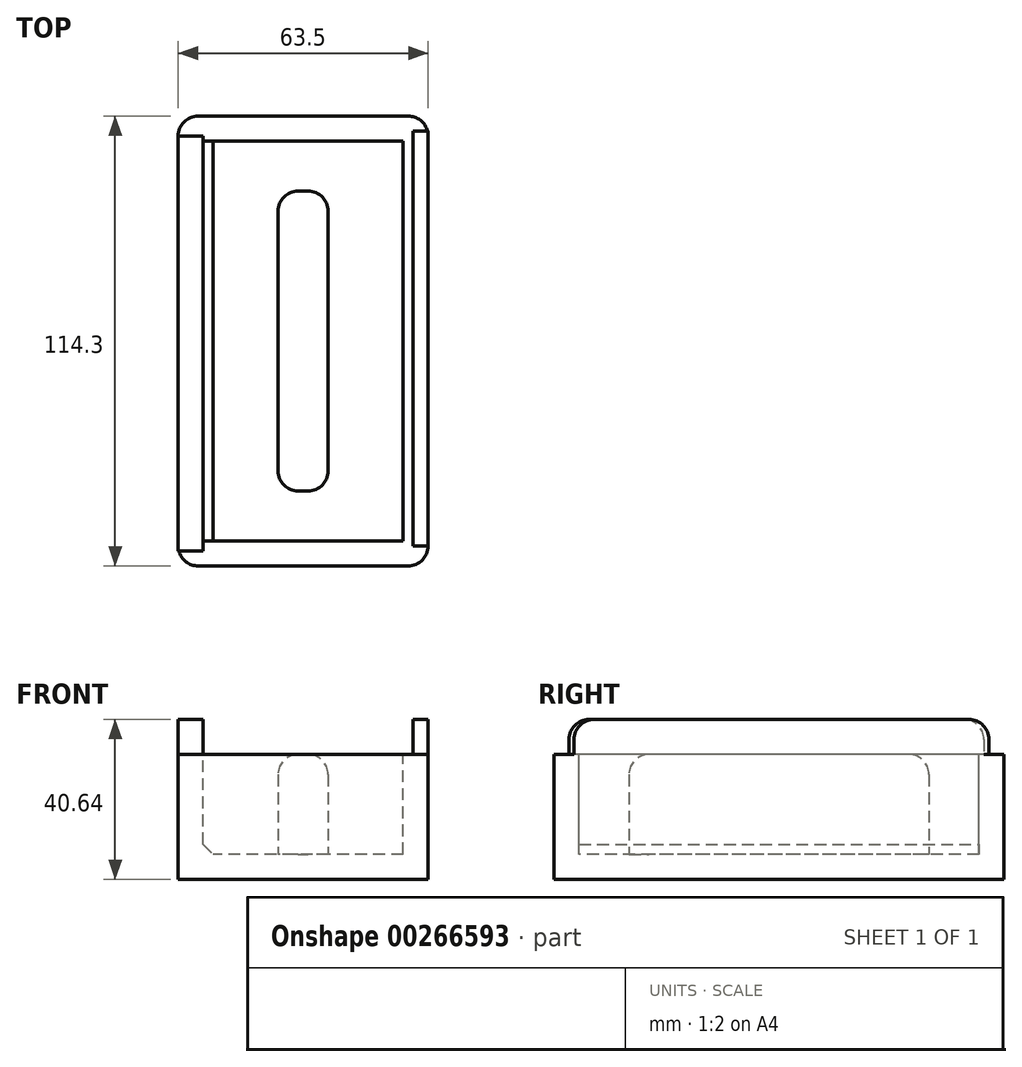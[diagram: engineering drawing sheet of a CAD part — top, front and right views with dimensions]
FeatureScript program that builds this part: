
annotation { "Feature Type Name" : "Feature", "Feature Type Description" : "" }
export const myFeature = defineFeature(function(context is Context, id is Id, definition is map)
    precondition{}
    {
        {
            var Q0;
            Q0=qCreatedBy(makeId("Top.planeOp"),FACE);
            var sketch = newSketch(context, id + "F0", { "sketchPlane" : qUnion([Q0])});
            skLineSegment(sketch, "E0.bottom", {"start": v(-31.75, -57.15) * mm, "end": v(31.75, -57.15) * mm});
            skLineSegment(sketch, "E0.top", {"start": v(-31.75, 57.15) * mm, "end": v(31.75, 57.15) * mm});
            skLineSegment(sketch, "E0.left", {"start": v(-31.75, -57.15) * mm, "end": v(-31.75, 57.15) * mm});
            skLineSegment(sketch, "E0.right", {"start": v(31.75, -57.15) * mm, "end": v(31.75, 57.15) * mm});
            skPoint(sketch, "E0.middle", {"position": v(0, 0) * mm});
            skSolve(sketch);
        }
        {
            var Q0;
            Q0=makeQuery(id+"F0.imprint","IMPRINT",FACE,{"disambiguationData":[TD([[makeQuery(id+"F0.imprint","IMPRINT",EDGE,{"derivedFrom":sQuery(id+"F0.wireOp",EDGE,"E0.bottom")}),1.0]])]});
            extrude(context, id + "F1", {"entities" : qUnion([Q0]), "depth" : 31.75 * mm});
        }
        {
            var Q0;
            Q0=makeQuery(id+"F1.opExtrude","CAP_FACE",FACE,{"disambiguationData":[OSD([sQuery(id+"F0.wireOp",EDGE,"E0.bottom"),sQuery(id+"F0.wireOp",EDGE,"E0.top"),sQuery(id+"F0.wireOp",EDGE,"E0.left"),sQuery(id+"F0.wireOp",EDGE,"E0.right")])],"isStart":false});
            var sketch = newSketch(context, id + "F2", { "sketchPlane" : qUnion([Q0])});
            skLineSegment(sketch, "E1.bottom", {"start": v(25.4, 50.8) * mm, "end": v(-25.4, 50.8) * mm});
            skLineSegment(sketch, "E1.top", {"start": v(25.4, -50.8) * mm, "end": v(-25.4, -50.8) * mm});
            skLineSegment(sketch, "E1.left", {"start": v(25.4, 50.8) * mm, "end": v(25.4, -50.8) * mm});
            skLineSegment(sketch, "E1.right", {"start": v(-25.4, 50.8) * mm, "end": v(-25.4, -50.8) * mm});
            skPoint(sketch, "E1.middle", {"position": v(0, 0) * mm});
            skSolve(sketch);
        }
        {
            var Q0;
            Q0 = qSketchRegion(id + "F2", true);
            extrude(context, id + "F3", {"entities" : qUnion([Q0]), "operationType" : NewBodyOperationType.REMOVE, "oppositeDirection" : true, "depth" : 25.4 * mm});
        }
        {
            var Q0;
            Q0=makeQuery(id+"F3.boolean.opBoolean","COPY",FACE,{"derivedFrom":makeQuery(id+"F3.opExtrude","CAP_FACE",FACE,{"disambiguationData":[OSD([sQuery(id+"F2.wireOp",EDGE,"E1.bottom"),sQuery(id+"F2.wireOp",EDGE,"E1.top"),sQuery(id+"F2.wireOp",EDGE,"E1.left"),sQuery(id+"F2.wireOp",EDGE,"E1.right")])],"isStart":false})});
            var sketch = newSketch(context, id + "F4", { "sketchPlane" : qUnion([Q0])});
            skLineSegment(sketch, "E2.bottom", {"start": v(-6.35, 38.1) * mm, "end": v(6.35, 38.1) * mm});
            skLineSegment(sketch, "E2.top", {"start": v(-6.35, -38.1) * mm, "end": v(6.35, -38.1) * mm});
            skLineSegment(sketch, "E2.left", {"start": v(-6.35, 38.1) * mm, "end": v(-6.35, -38.1) * mm});
            skLineSegment(sketch, "E2.right", {"start": v(6.35, 38.1) * mm, "end": v(6.35, -38.1) * mm});
            skPoint(sketch, "E2.middle", {"position": v(0, 0) * mm});
            skSolve(sketch);
        }
        {
            var Q0;
            Q0=makeQuery(id+"F4.imprint","IMPRINT",FACE,{"disambiguationData":[TD([[makeQuery(id+"F4.imprint","IMPRINT",EDGE,{"derivedFrom":sQuery(id+"F4.wireOp",EDGE,"E2.bottom")}),-1.0]])]});
            extrude(context, id + "F5", {"entities" : qUnion([Q0]), "operationType" : NewBodyOperationType.ADD, "depth" : 25.4 * mm});
        }
        {
            var Q0;
            Q0=makeQuery(id+"F5.opExtrude","SWEPT_EDGE",EDGE,{"disambiguationData":[OSD([sQuery(id+"F4.wireOp",EDGE,"E2.top"),sQuery(id+"F4.wireOp",EDGE,"E2.right")])]});
            var Q1;
            Q1=makeQuery(id+"F5.opExtrude","SWEPT_EDGE",EDGE,{"disambiguationData":[OSD([sQuery(id+"F4.wireOp",EDGE,"E2.top"),sQuery(id+"F4.wireOp",EDGE,"E2.left")])]});
            var Q2;
            Q2=makeQuery(id+"F5.opExtrude","SWEPT_EDGE",EDGE,{"disambiguationData":[OSD([sQuery(id+"F4.wireOp",EDGE,"E2.bottom"),sQuery(id+"F4.wireOp",EDGE,"E2.right")])]});
            var Q3;
            Q3=makeQuery(id+"F5.opExtrude","SWEPT_EDGE",EDGE,{"disambiguationData":[OSD([sQuery(id+"F4.wireOp",EDGE,"E2.bottom"),sQuery(id+"F4.wireOp",EDGE,"E2.left")])]});
            fillet(context, id + "F6", {"entities" : qUnion([Q0, Q1, Q2, Q3]), "radius" : 5.08 * mm, "tangentPropagation" : true, "allowEdgeOverflow" : false});
        }
        {
            var Q0;
            Q0=makeQuery(id+"F3.boolean.opBoolean","COPY",EDGE,{"derivedFrom":makeQuery(id+"F3.opExtrude","CAP_EDGE",EDGE,{"disambiguationData":[OSD([sQuery(id+"F2.wireOp",EDGE,"E1.right")])],"isStart":false})});
            var Q1;
            Q1=makeQuery(id+"F3.boolean.opBoolean","COPY",EDGE,{"derivedFrom":makeQuery(id+"F3.opExtrude","CAP_EDGE",EDGE,{"disambiguationData":[OSD([sQuery(id+"F2.wireOp",EDGE,"E1.bottom")])],"isStart":true})});
            var Q2;
            Q2=makeQuery(id+"F3.boolean.opBoolean","COPY",EDGE,{"derivedFrom":makeQuery(id+"F3.opExtrude","CAP_EDGE",EDGE,{"disambiguationData":[OSD([sQuery(id+"F2.wireOp",EDGE,"E1.left")])],"isStart":true})});
            var Q3;
            Q3=makeQuery(id+"F3.boolean.opBoolean","COPY",EDGE,{"derivedFrom":makeQuery(id+"F3.opExtrude","CAP_EDGE",EDGE,{"disambiguationData":[OSD([sQuery(id+"F2.wireOp",EDGE,"E1.top")])],"isStart":true})});
            chamfer(context, id + "F7", {"entities" : qUnion([Q0, Q1, Q2, Q3]), "width" : 2.54 * mm, "tangentPropagation" : true});
        }
        {
            var Q0;
            Q0=makeQuery(id+"F5.opExtrude","CAP_EDGE",EDGE,{"disambiguationData":[OSD([sQuery(id+"F4.wireOp",EDGE,"E2.right")])],"isStart":false});
            var Q1;
            Q1=makeQuery(id+"F5.opExtrude","CAP_EDGE",EDGE,{"disambiguationData":[OSD([sQuery(id+"F4.wireOp",EDGE,"E2.left")])],"isStart":false});
            fillet(context, id + "F8", {"entities" : qUnion([Q0, Q1]), "radius" : 5.08 * mm, "tangentPropagation" : true, "allowEdgeOverflow" : false});
        }
        {
            var Q0;
            Q0=makeQuery(id+"F1.opExtrude","SWEPT_EDGE",EDGE,{"disambiguationData":[OSD([sQuery(id+"F0.wireOp",EDGE,"E0.bottom"),sQuery(id+"F0.wireOp",EDGE,"E0.left")])]});
            var Q1;
            Q1=makeQuery(id+"F1.opExtrude","SWEPT_EDGE",EDGE,{"disambiguationData":[OSD([sQuery(id+"F0.wireOp",EDGE,"E0.bottom"),sQuery(id+"F0.wireOp",EDGE,"E0.right")])]});
            var Q2;
            Q2=makeQuery(id+"F1.opExtrude","SWEPT_EDGE",EDGE,{"disambiguationData":[OSD([sQuery(id+"F0.wireOp",EDGE,"E0.top"),sQuery(id+"F0.wireOp",EDGE,"E0.right")])]});
            var Q3;
            Q3=makeQuery(id+"F1.opExtrude","SWEPT_EDGE",EDGE,{"disambiguationData":[OSD([sQuery(id+"F0.wireOp",EDGE,"E0.top"),sQuery(id+"F0.wireOp",EDGE,"E0.left")])]});
            fillet(context, id + "F9", {"entities" : qUnion([Q0, Q1, Q2, Q3]), "radius" : 5.08 * mm, "tangentPropagation" : true, "allowEdgeOverflow" : false});
        }
        {
            var Q0;
            Q0=makeQuery(id+"F1.opExtrude","CAP_FACE",FACE,{"disambiguationData":[OSD([sQuery(id+"F0.wireOp",EDGE,"E0.bottom"),sQuery(id+"F0.wireOp",EDGE,"E0.top"),sQuery(id+"F0.wireOp",EDGE,"E0.left"),sQuery(id+"F0.wireOp",EDGE,"E0.right")])],"isStart":false});
            var sketch = newSketch(context, id + "F10", { "sketchPlane" : qUnion([Q0])});
            skLineSegment(sketch, "E3.bottom", {"start": v(-31.75, 52.07) * mm, "end": v(-25.4, 52.07) * mm});
            skLineSegment(sketch, "E3.top", {"start": v(-31.75, -53.34) * mm, "end": v(-25.4, -53.34) * mm});
            skLineSegment(sketch, "E3.left", {"start": v(-31.75, 52.07) * mm, "end": v(-31.75, -53.34) * mm});
            skLineSegment(sketch, "E3.right", {"start": v(-25.4, 52.07) * mm, "end": v(-25.4, -53.34) * mm});
            skLineSegment(sketch, "E4.bottom", {"start": v(27.94, 53.34) * mm, "end": v(31.75, 53.34) * mm});
            skLineSegment(sketch, "E4.top", {"start": v(27.94, -52.07) * mm, "end": v(31.75, -52.07) * mm});
            skLineSegment(sketch, "E4.left", {"start": v(27.94, 53.34) * mm, "end": v(27.94, -52.07) * mm});
            skLineSegment(sketch, "E4.right", {"start": v(31.75, 53.34) * mm, "end": v(31.75, -52.07) * mm});
            skSolve(sketch);
        }
        {
            var Q0;
            Q0 = qSketchRegion(id + "F10", true);
            extrude(context, id + "F11", {"entities" : qUnion([Q0]), "operationType" : NewBodyOperationType.ADD, "depth" : 8.9 * mm});
        }
        {
            var Q0;
            Q0=makeQuery(id+"F11.opExtrude","CAP_EDGE",EDGE,{"disambiguationData":[OSD([sQuery(id+"F10.wireOp",EDGE,"E3.top")])],"isStart":false});
            var Q1;
            Q1=makeQuery(id+"F11.opExtrude","CAP_EDGE",EDGE,{"disambiguationData":[OSD([sQuery(id+"F10.wireOp",EDGE,"E4.top")])],"isStart":false});
            var Q2;
            Q2=makeQuery(id+"F11.opExtrude","CAP_EDGE",EDGE,{"disambiguationData":[OSD([sQuery(id+"F10.wireOp",EDGE,"E3.bottom")])],"isStart":false});
            var Q3;
            Q3=makeQuery(id+"F11.opExtrude","CAP_EDGE",EDGE,{"disambiguationData":[OSD([sQuery(id+"F10.wireOp",EDGE,"E4.bottom")])],"isStart":false});
            fillet(context, id + "F12", {"entities" : qUnion([Q0, Q1, Q2, Q3]), "radius" : 5.08 * mm, "tangentPropagation" : true, "allowEdgeOverflow" : false});
        }
    });
